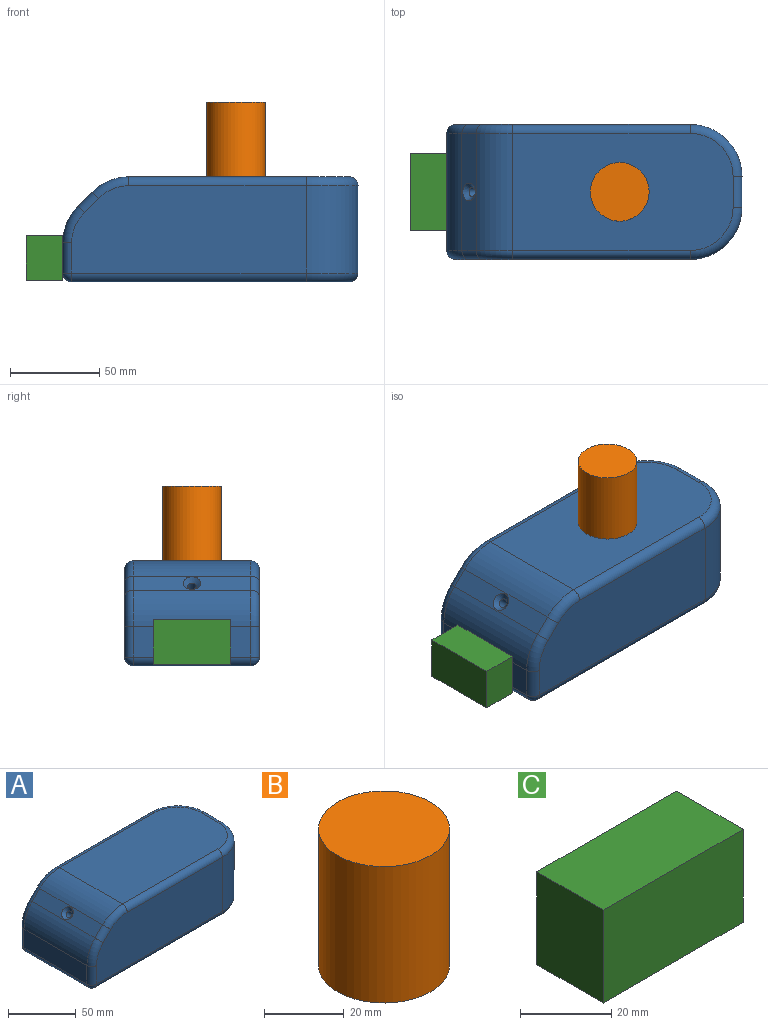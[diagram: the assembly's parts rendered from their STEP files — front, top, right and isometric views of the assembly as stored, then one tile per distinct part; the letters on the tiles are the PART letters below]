
ASSEMBLY  parts=3 mates=2
PART A: 34 faces, bbox 171.7x81.6x66 mm
  f0: plane 65.74x16.93mm, normal (-1,0,0), area 1113.2mm2, adj f10,f13,f25,f32
  f1: plane 131.69x49mm, normal (0,-1,0), area 6184.3mm2, adj f11,f21,f22,f23,f24,f25,f31
  f2: plane 49x17.48mm, normal (1,0,0), area 856.5mm2, adj f11,f12,f19,f27
  f3: plane 131.69x49mm, normal (0,1,0), area 6184.3mm2, adj f12,f13,f14,f15,f16,f17,f28
  f4: plane 123.76x65.74mm, normal (0,0,1), area 7885.6mm2, adj f9,f17,f18,f19,f20,f21
  f5: plane 156.87x66.79mm, normal (0,0,-1), area 9965.7mm2, adj f7,f26,f27,f28,f29,f31,f32
  f6: plane 65.74x7.94mm, normal (-0.71,0,0.71), area 659.3mm2, adj f8,f9,f10,f15,f23
  f7: cylinder r=2.5mm len=50.04mm, axis (-0.71,0,0.71), area 993.7mm2, adj f5,f8
  f8: cone r=2.5mm half-angle=45deg, axis (-0.71,0,0.71), area 83.3mm2, adj f6,f7
  f9: cylinder r=29.13mm len=65.74mm, axis (0,1,0), area 1503.9mm2, adj f4,f6,f16,f22
  f10: cylinder r=29.13mm len=65.74mm, axis (0,-1,0), area 1503.9mm2, adj f0,f6,f14,f24
  f11: cylinder r=29.13mm len=49mm, axis (0,0,-1), area 2242mm2, adj f1,f2,f20,f29
  f12: cylinder r=29.13mm len=49mm, axis (0,0,1), area 2242mm2, adj f2,f3,f18,f26
  f13: cylinder r=5mm len=16.93mm, axis (0,0,-1), area 133mm2, adj f0,f3,f14,f30
  f14: torus R=24.13mm, axis (0,1,0), area 168.5mm2, adj f3,f10,f13,f15
  f15: cylinder r=5mm len=11.47mm, axis (-0.71,0,-0.71), area 88.2mm2, adj f3,f6,f14,f16
  f16: torus R=24.13mm, axis (0,1,0), area 168.5mm2, adj f3,f9,f15,f17
  f17: cylinder r=5mm len=99.63mm, axis (1,0,0), area 782.5mm2, adj f3,f4,f16,f18
  f18: torus R=24.13mm, axis (0,0,1), area 336.9mm2, adj f4,f12,f17,f19
  f19: cylinder r=5mm len=17.48mm, axis (0,-1,0), area 137.3mm2, adj f2,f4,f18,f20
  f20: torus R=24.13mm, axis (0,0,1), area 336.9mm2, adj f4,f11,f19,f21
  f21: cylinder r=5mm len=99.63mm, axis (-1,0,0), area 782.5mm2, adj f1,f4,f20,f22
  f22: torus R=24.13mm, axis (0,1,0), area 168.5mm2, adj f1,f9,f21,f23
  f23: cylinder r=5mm len=11.47mm, axis (-0.71,0,-0.71), area 88.2mm2, adj f1,f6,f22,f24
  f24: torus R=24.13mm, axis (0,1,0), area 168.5mm2, adj f1,f10,f23,f25
  f25: cylinder r=5mm len=16.93mm, axis (0,0,1), area 133mm2, adj f0,f1,f24,f33
  f26: torus R=24.13mm, axis (0,0,1), area 336.9mm2, adj f5,f12,f27,f28
  f27: cylinder r=5mm len=17.48mm, axis (0,1,0), area 137.3mm2, adj f2,f5,f26,f29
  f28: cylinder r=5mm len=131.69mm, axis (-1,0,0), area 1034.3mm2, adj f3,f5,f26,f30
  f29: torus R=24.13mm, axis (0,0,1), area 336.9mm2, adj f5,f11,f27,f31
  f30: sphere r=5mm, area 39.3mm2, adj f13,f28,f32
  f31: cylinder r=5mm len=131.69mm, axis (1,0,0), area 1034.3mm2, adj f1,f5,f29,f33
  f32: cylinder r=5mm len=65.74mm, axis (0,-1,0), area 516.3mm2, adj f0,f5,f30,f33
  f33: sphere r=5mm, area 39.3mm2, adj f25,f31,f32
PART B: 3 faces, bbox 33x33x42 mm
  f0: cylinder r=16.48mm len=42mm, axis (0,0,-1), area 4349.9mm2, adj f1,f2
  f1: plane 32.97x32.97mm, normal (0,0,1), area 853.6mm2, adj f0
  f2: plane 32.97x32.97mm, normal (0,0,-1), area 853.6mm2, adj f0
PART C: 6 faces, bbox 43.5x20.6x25 mm
  f0: plane 25x20.64mm, normal (-1,0,0), area 516mm2, adj f1,f3,f4,f5
  f1: plane 43.47x25mm, normal (0,-1,0), area 1086.7mm2, adj f0,f2,f4,f5
  f2: plane 25x20.64mm, normal (1,0,0), area 516mm2, adj f1,f3,f4,f5
  f3: plane 43.47x25mm, normal (0,1,0), area 1086.7mm2, adj f0,f2,f4,f5
  f4: plane 43.47x20.64mm, normal (0,0,1), area 897.3mm2, adj f0,f1,f2,f3
  f5: plane 43.47x20.64mm, normal (0,0,-1), area 897.3mm2, adj f0,f1,f2,f3
PLACE A rot(axis=(-0.05,0.99,-0.16),0deg) t=(7.7,-1.96,-7.97)mm
PLACE B rot(axis=(-0.05,0.99,-0.16),0deg) t=(19.39,-79.96,51.03)mm
PLACE C rot(axis=(0,0,1),90deg) t=(-136.79,35.24,-7)mm
MATE slider B.f0 <-> A.f4  axis (0,0,-1) through (36.37,-11.89,51.03)mm
MATE slider C.f1 <-> A.f0  axis (1,0,0) through (-60.78,-11.89,5.5)mm
